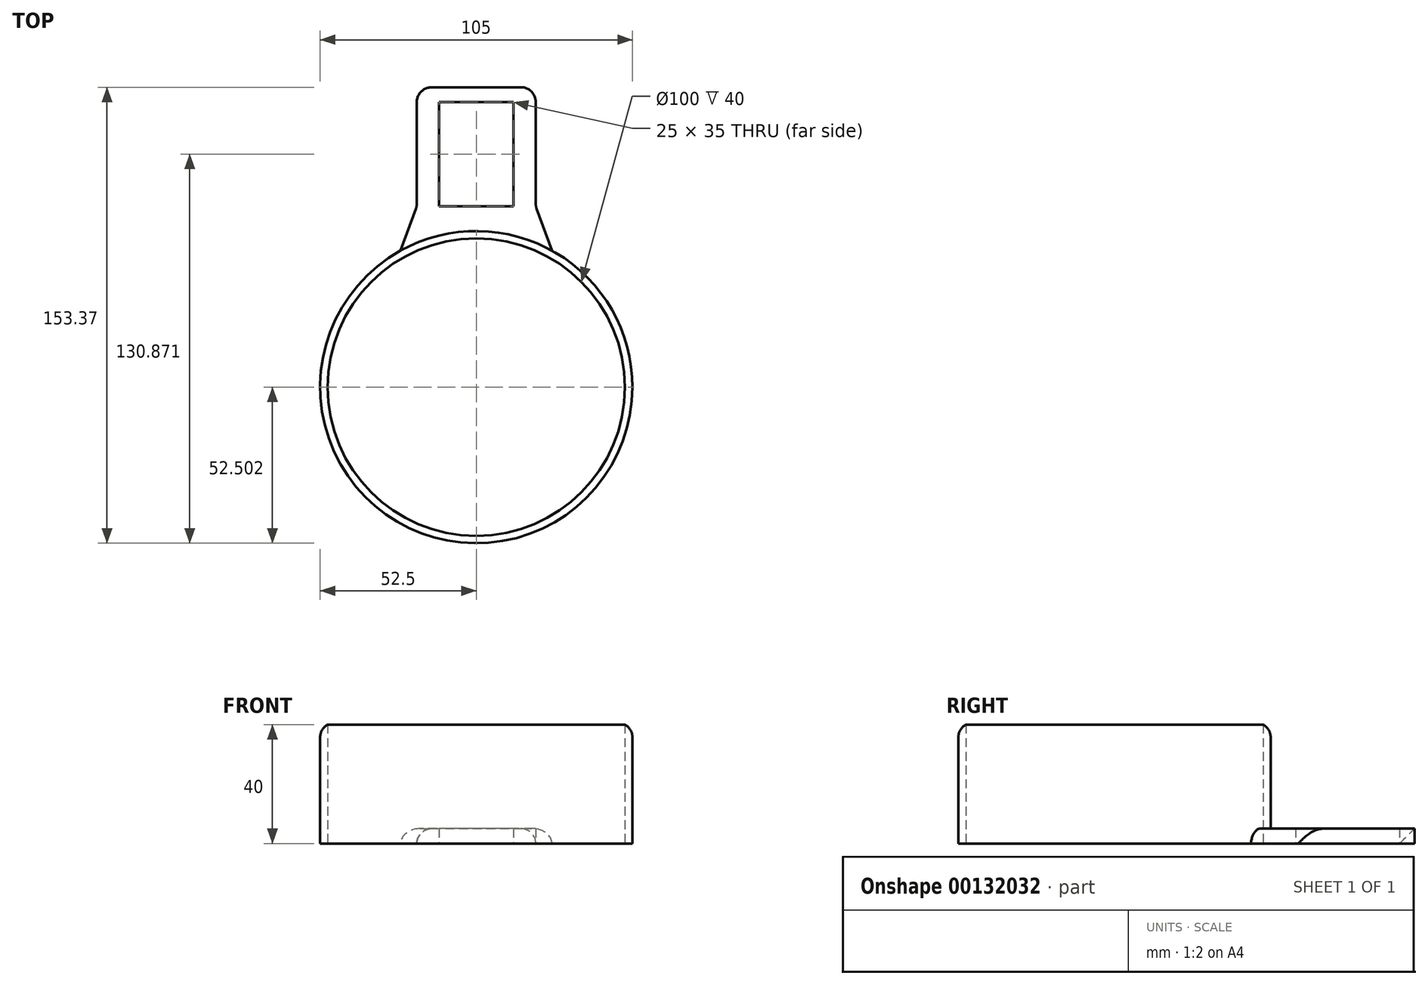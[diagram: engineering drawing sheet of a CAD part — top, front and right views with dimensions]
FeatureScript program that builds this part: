
annotation { "Feature Type Name" : "Feature", "Feature Type Description" : "" }
export const myFeature = defineFeature(function(context is Context, id is Id, definition is map)
    precondition{}
    {
        {
            var Q0;
            Q0=qCreatedBy(makeId("Top.planeOp"),FACE);
            var sketch = newSketch(context, id + "F0", { "sketchPlane" : qUnion([Q0])});
            skCircle(sketch, "E0", {"center": v(0, 0) * mm, "radius": 50 * mm});
            skCircle(sketch, "E1.0", {"center": v(0, 0) * mm, "radius": 52.5 * mm});
            skSolve(sketch);
        }
        {
            var Q0;
            Q0=qCreatedBy(makeId("Top.planeOp"),FACE);
            var sketch = newSketch(context, id + "F1", { "sketchPlane" : qUnion([Q0])});
            skLineSegment(sketch, "E2.bottom", {"start": v(12.5, 32.24) * mm, "end": v(-12.5, 32.24) * mm});
            skLineSegment(sketch, "E2.top", {"start": v(12.5, 67.24) * mm, "end": v(-12.5, 67.24) * mm});
            skLineSegment(sketch, "E2.left", {"start": v(12.5, 32.24) * mm, "end": v(12.5, 67.24) * mm});
            skLineSegment(sketch, "E2.right", {"start": v(-12.5, 32.24) * mm, "end": v(-12.5, 67.24) * mm});
            skPoint(sketch, "E2.middle", {"position": v(0, 49.74) * mm});
            skCircle(sketch, "E3", {"center": v(0, -28.63) * mm, "radius": 52.5 * mm});
            skLineSegment(sketch, "E4", {"start": v(-25.44, 17.3) * mm, "end": v(-20, 32.24) * mm});
            skLineSegment(sketch, "E5", {"start": v(-20, 32.24) * mm, "end": v(-20, 72.24) * mm});
            skLineSegment(sketch, "E6", {"start": v(-20, 72.24) * mm, "end": v(20, 72.24) * mm});
            skLineSegment(sketch, "E7", {"start": v(20, 72.24) * mm, "end": v(20, 32.24) * mm});
            skLineSegment(sketch, "E8", {"start": v(20, 32.24) * mm, "end": v(25.44, 17.3) * mm});
            skCircle(sketch, "E9.0", {"center": v(0, -28.63) * mm, "radius": 50 * mm});
            skSolve(sketch);
        }
        {
            var Q0;
            Q0=makeQuery(id+"F1.imprint","IMPRINT",FACE,{"disambiguationData":[TD([[makeQuery(id+"F1.imprint","IMPRINT",EDGE,{"derivedFrom":sQuery(id+"F1.wireOp",EDGE,"E2.bottom")}),1.0]])]});
            extrude(context, id + "F2", {"entities" : qUnion([Q0]), "depth" : 5 * mm});
        }
        {
            var Q0;
            Q0=makeQuery(id+"F1.imprint","IMPRINT",FACE,{"disambiguationData":[TD([[makeQuery(id+"F1.imprint","IMPRINT",EDGE,{"derivedFrom":sQuery(id+"F1.wireOp",EDGE,"E9.0")}),-1.0]])]});
            extrude(context, id + "F3", {"entities" : qUnion([Q0]), "operationType" : NewBodyOperationType.ADD, "depth" : 40 * mm});
        }
        {
            var Q0;
            Q0=makeQuery(id+"F3.opExtrude","CAP_EDGE",EDGE,{"disambiguationData":[OSD([sQuery(id+"F1.wireOp",EDGE,"E3")])],"isStart":false});
            var Q1;
            Q1=makeQuery(id+"F2.opExtrude","SWEPT_EDGE",EDGE,{"disambiguationData":[OSD([sQuery(id+"F1.wireOp",EDGE,"E4"),sQuery(id+"F1.wireOp",EDGE,"E5")])]});
            fillet(context, id + "F4", {"entities" : qUnion([Q0, Q1]), "radius" : 5 * mm, "tangentPropagation" : true, "allowEdgeOverflow" : false});
        }
        {
            var Q0;
            Q0=makeQuery(id+"F2.opExtrude","SWEPT_EDGE",EDGE,{"disambiguationData":[OSD([sQuery(id+"F1.wireOp",EDGE,"E5"),sQuery(id+"F1.wireOp",EDGE,"E6")])]});
            var Q1;
            Q1=makeQuery(id+"F2.opExtrude","SWEPT_EDGE",EDGE,{"disambiguationData":[OSD([sQuery(id+"F1.wireOp",EDGE,"E6"),sQuery(id+"F1.wireOp",EDGE,"E7")])]});
            var Q2;
            Q2=makeQuery(id+"F2.opExtrude","SWEPT_EDGE",EDGE,{"disambiguationData":[OSD([sQuery(id+"F1.wireOp",EDGE,"E7"),sQuery(id+"F1.wireOp",EDGE,"E8")])]});
            var Q3;
            Q3=makeQuery(id+"F2.opExtrude","SWEPT_EDGE",EDGE,{"disambiguationData":[OSD([sQuery(id+"F1.wireOp",EDGE,"E3"),sQuery(id+"F1.wireOp",EDGE,"E8")])]});
            var Q4;
            Q4=makeQuery(id+"F2.opExtrude","CAP_EDGE",EDGE,{"disambiguationData":[OSD([sQuery(id+"F1.wireOp",EDGE,"E8")])],"isStart":false});
            var Q5;
            Q5=makeQuery(id+"F2.opExtrude","SWEPT_EDGE",EDGE,{"disambiguationData":[OSD([sQuery(id+"F1.wireOp",EDGE,"E3"),sQuery(id+"F1.wireOp",EDGE,"E4")])]});
            var Q6;
            Q6=makeQuery(id+"F2.opExtrude","CAP_EDGE",EDGE,{"disambiguationData":[OSD([sQuery(id+"F1.wireOp",EDGE,"E5")])],"isStart":false});
            fillet(context, id + "F5", {"entities" : qUnion([Q0, Q1, Q2, Q3, Q4, Q5, Q6]), "radius" : 5 * mm, "tangentPropagation" : true, "allowEdgeOverflow" : false});
        }
    });
